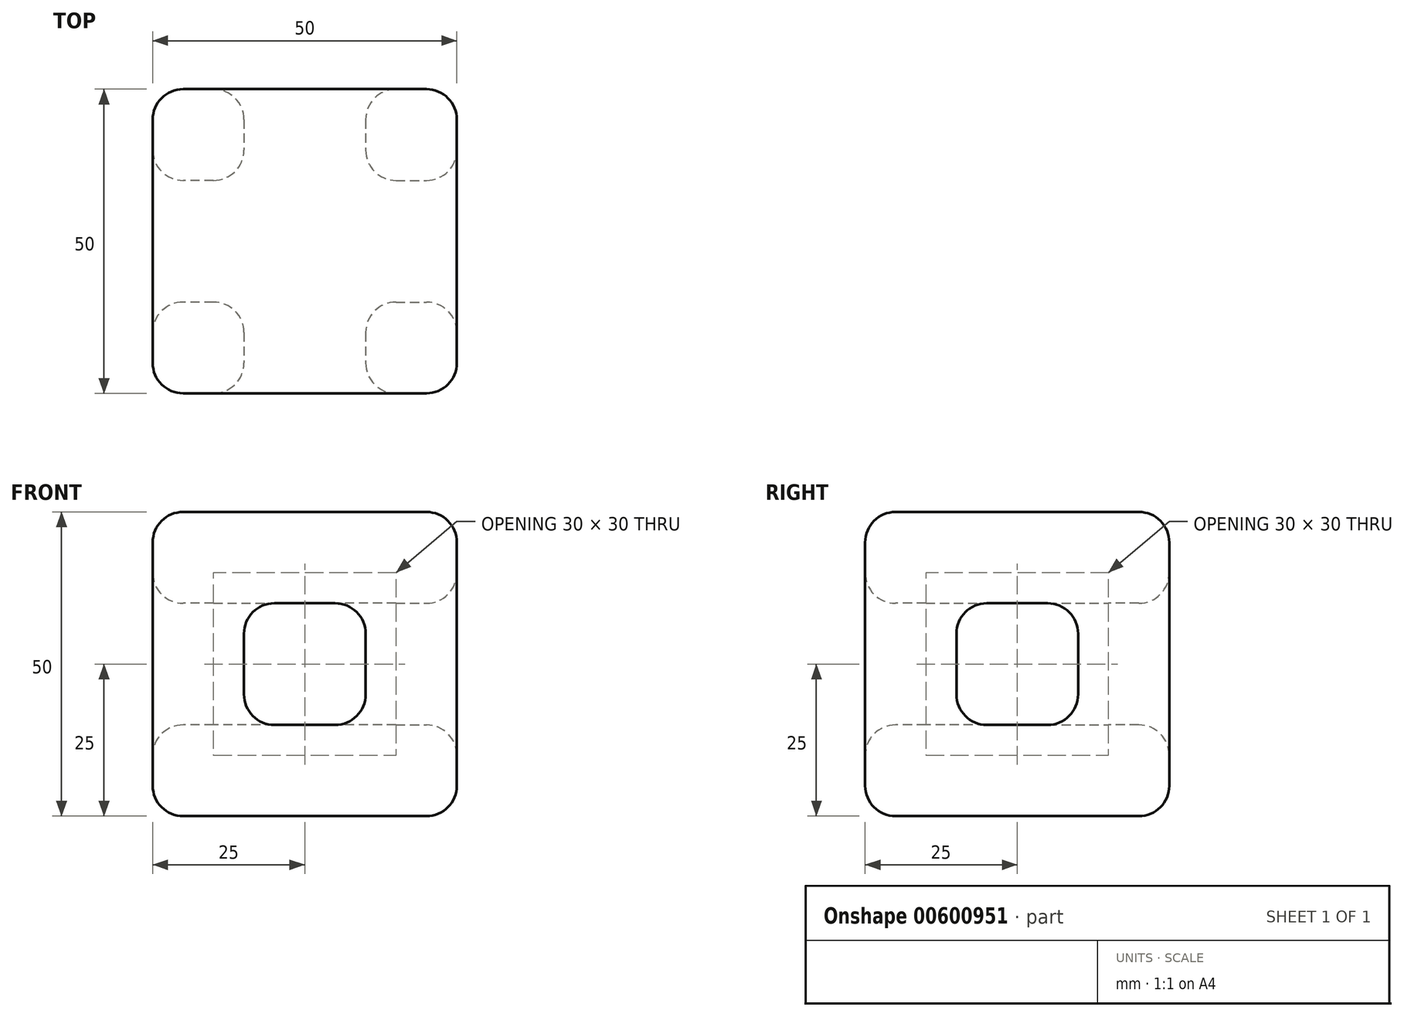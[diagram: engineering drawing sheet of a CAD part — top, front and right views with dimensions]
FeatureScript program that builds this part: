
annotation { "Feature Type Name" : "Feature", "Feature Type Description" : "" }
export const myFeature = defineFeature(function(context is Context, id is Id, definition is map)
    precondition{}
    {
        {
            var Q0;
            Q0=qCreatedBy(makeId("Front.planeOp"),FACE);
            var sketch = newSketch(context, id + "F0", { "sketchPlane" : qUnion([Q0])});
            skLineSegment(sketch, "E0.bottom", {"start": v(25, -25) * mm, "end": v(-25, -25) * mm});
            skLineSegment(sketch, "E0.top", {"start": v(25, 25) * mm, "end": v(-25, 25) * mm});
            skLineSegment(sketch, "E0.left", {"start": v(25, -25) * mm, "end": v(25, 25) * mm});
            skLineSegment(sketch, "E0.right", {"start": v(-25, -25) * mm, "end": v(-25, 25) * mm});
            skPoint(sketch, "E0.middle", {"position": v(0, 0) * mm});
            skSolve(sketch);
        }
        {
            var Q0;
            Q0 = qSketchRegion(id + "F0", true);
            extrude(context, id + "F1", {"entities" : qUnion([Q0]), "endBound" : BoundingType.SYMMETRIC, "depth" : 50 * mm, "offsetDistance" : 25 * mm});
        }
        {
            var Q0;
            Q0=makeQuery(id+"F1.opExtrude","CAP_FACE",FACE,{"disambiguationData":[OSD([sQuery(id+"F0.wireOp",EDGE,"E0.bottom"),sQuery(id+"F0.wireOp",EDGE,"E0.top"),sQuery(id+"F0.wireOp",EDGE,"E0.left"),sQuery(id+"F0.wireOp",EDGE,"E0.right")])],"isStart":false});
            var sketch = newSketch(context, id + "F2", { "sketchPlane" : qUnion([Q0])});
            skLineSegment(sketch, "E1.bottom", {"start": v(-10, 10) * mm, "end": v(10, 10) * mm});
            skLineSegment(sketch, "E1.top", {"start": v(-10, -10) * mm, "end": v(10, -10) * mm});
            skLineSegment(sketch, "E1.left", {"start": v(-10, 10) * mm, "end": v(-10, -10) * mm});
            skLineSegment(sketch, "E1.right", {"start": v(10, 10) * mm, "end": v(10, -10) * mm});
            skPoint(sketch, "E1.middle", {"position": v(0, 0) * mm});
            skSolve(sketch);
        }
        {
            var Q0;
            Q0=makeQuery(id+"F2.imprint","IMPRINT",FACE,{"disambiguationData":[TD([[makeQuery(id+"F2.imprint","IMPRINT",EDGE,{"derivedFrom":sQuery(id+"F2.wireOp",EDGE,"E1.bottom")}),-1.0]])]});
            extrude(context, id + "F3", {"entities" : qUnion([Q0]), "operationType" : NewBodyOperationType.REMOVE, "endBound" : BoundingType.UP_TO_NEXT, "oppositeDirection" : true, "depth" : 25 * mm, "offsetDistance" : 25 * mm});
        }
        {
            var Q0;
            Q0=makeQuery(id+"F1.opExtrude","SWEPT_FACE",FACE,{"disambiguationData":[OSD([sQuery(id+"F0.wireOp",EDGE,"E0.left")])]});
            var sketch = newSketch(context, id + "F4", { "sketchPlane" : qUnion([Q0])});
            skLineSegment(sketch, "E2.bottom", {"start": v(-10, 10) * mm, "end": v(10, 10) * mm});
            skLineSegment(sketch, "E2.top", {"start": v(-10, -10) * mm, "end": v(10, -10) * mm});
            skLineSegment(sketch, "E2.left", {"start": v(-10, 10) * mm, "end": v(-10, -10) * mm});
            skLineSegment(sketch, "E2.right", {"start": v(10, 10) * mm, "end": v(10, -10) * mm});
            skPoint(sketch, "E2.middle", {"position": v(0, 0) * mm});
            skSolve(sketch);
        }
        {
            var Q0;
            Q0=makeQuery(id+"F4.imprint","IMPRINT",FACE,{"disambiguationData":[TD([[makeQuery(id+"F4.imprint","IMPRINT",EDGE,{"derivedFrom":sQuery(id+"F4.wireOp",EDGE,"E2.bottom")}),-1.0]])]});
            extrude(context, id + "F5", {"entities" : qUnion([Q0]), "operationType" : NewBodyOperationType.REMOVE, "endBound" : BoundingType.UP_TO_NEXT, "oppositeDirection" : true, "depth" : 25 * mm, "offsetDistance" : 25 * mm});
        }
        {
            var Q0;
            Q0=makeQuery(id+"F1.opExtrude","SWEPT_FACE",FACE,{"disambiguationData":[OSD([sQuery(id+"F0.wireOp",EDGE,"E0.right")])]});
            var sketch = newSketch(context, id + "F6", { "sketchPlane" : qUnion([Q0])});
            skLineSegment(sketch, "E3.bottom", {"start": v(-10, 10) * mm, "end": v(10, 10) * mm});
            skLineSegment(sketch, "E3.top", {"start": v(-10, -10) * mm, "end": v(10, -10) * mm});
            skLineSegment(sketch, "E3.left", {"start": v(-10, 10) * mm, "end": v(-10, -10) * mm});
            skLineSegment(sketch, "E3.right", {"start": v(10, 10) * mm, "end": v(10, -10) * mm});
            skPoint(sketch, "E3.middle", {"position": v(0, 0) * mm});
            skSolve(sketch);
        }
        {
            var Q0;
            Q0=makeQuery(id+"F6.imprint","IMPRINT",FACE,{"disambiguationData":[TD([[makeQuery(id+"F6.imprint","IMPRINT",EDGE,{"derivedFrom":sQuery(id+"F6.wireOp",EDGE,"E3.bottom")}),-1.0]])]});
            extrude(context, id + "F7", {"entities" : qUnion([Q0]), "operationType" : NewBodyOperationType.REMOVE, "endBound" : BoundingType.UP_TO_NEXT, "oppositeDirection" : true, "depth" : 25 * mm, "offsetDistance" : 25 * mm});
        }
        {
            var Q0;
            Q0=makeQuery(id+"F7.boolean.opBoolean","COPY",EDGE,{"derivedFrom":makeQuery(id+"F7.opExtrude","SWEPT_EDGE",EDGE,{"disambiguationData":[OSD([sQuery(id+"F6.wireOp",EDGE,"E3.bottom"),sQuery(id+"F6.wireOp",EDGE,"E3.right")])]})});
            var Q1;
            Q1=makeQuery(id+"F5.boolean.opBoolean","COPY",EDGE,{"derivedFrom":makeQuery(id+"F5.opExtrude","SWEPT_EDGE",EDGE,{"disambiguationData":[OSD([sQuery(id+"F4.wireOp",EDGE,"E2.bottom"),sQuery(id+"F4.wireOp",EDGE,"E2.left")])]})});
            var Q2;
            Q2=makeQuery(id+"F3.boolean.opBoolean","COPY",EDGE,{"derivedFrom":makeQuery(id+"F3.opExtrude","CAP_EDGE",EDGE,{"disambiguationData":[OSD([sQuery(id+"F2.wireOp",EDGE,"E1.right")])],"isStart":true})});
            var Q3;
            Q3=makeQuery(id+"F1.opExtrude","CAP_EDGE",EDGE,{"disambiguationData":[OSD([sQuery(id+"F0.wireOp",EDGE,"E0.bottom")])],"isStart":false});
            var Q4;
            Q4=makeQuery(id+"F1.opExtrude","CAP_FACE",FACE,{"disambiguationData":[OSD([sQuery(id+"F0.wireOp",EDGE,"E0.bottom"),sQuery(id+"F0.wireOp",EDGE,"E0.top"),sQuery(id+"F0.wireOp",EDGE,"E0.left"),sQuery(id+"F0.wireOp",EDGE,"E0.right")])],"isStart":false});
            var Q5;
            Q5=makeQuery(id+"F7.boolean.opBoolean","COPY",EDGE,{"derivedFrom":makeQuery(id+"F7.opExtrude","SWEPT_EDGE",EDGE,{"disambiguationData":[OSD([sQuery(id+"F6.wireOp",EDGE,"E3.top"),sQuery(id+"F6.wireOp",EDGE,"E3.right")])]})});
            var Q6;
            Q6=makeQuery(id+"F3.boolean.opBoolean","COPY",EDGE,{"derivedFrom":makeQuery(id+"F3.opExtrude","CAP_EDGE",EDGE,{"disambiguationData":[OSD([sQuery(id+"F2.wireOp",EDGE,"E1.bottom")])],"isStart":true})});
            var Q7;
            Q7=makeQuery(id+"F1.opExtrude","SWEPT_EDGE",EDGE,{"disambiguationData":[OSD([sQuery(id+"F0.wireOp",EDGE,"E0.top"),sQuery(id+"F0.wireOp",EDGE,"E0.right")])]});
            var Q8;
            Q8=makeQuery(id+"F1.opExtrude","CAP_EDGE",EDGE,{"disambiguationData":[OSD([sQuery(id+"F0.wireOp",EDGE,"E0.right")])],"isStart":false});
            var Q9;
            Q9=makeQuery(id+"F3.boolean.opBoolean","COPY",EDGE,{"derivedFrom":makeQuery(id+"F3.opExtrude","CAP_EDGE",EDGE,{"disambiguationData":[OSD([sQuery(id+"F2.wireOp",EDGE,"E1.top")])],"isStart":true})});
            var Q10;
            Q10=makeQuery(id+"F1.opExtrude","CAP_EDGE",EDGE,{"disambiguationData":[OSD([sQuery(id+"F0.wireOp",EDGE,"E0.top")])],"isStart":false});
            var Q11;
            Q11=makeQuery(id+"F5.boolean.opBoolean","COPY",EDGE,{"derivedFrom":makeQuery(id+"F5.opExtrude","SWEPT_EDGE",EDGE,{"disambiguationData":[OSD([sQuery(id+"F4.wireOp",EDGE,"E2.top"),sQuery(id+"F4.wireOp",EDGE,"E2.left")])]})});
            var Q12;
            Q12=makeQuery(id+"F3.boolean.opBoolean","COPY",EDGE,{"derivedFrom":makeQuery(id+"F3.opExtrude","CAP_EDGE",EDGE,{"disambiguationData":[OSD([sQuery(id+"F2.wireOp",EDGE,"E1.left")])],"isStart":true})});
            var Q13;
            Q13=makeQuery(id+"F1.opExtrude","CAP_EDGE",EDGE,{"disambiguationData":[OSD([sQuery(id+"F0.wireOp",EDGE,"E0.left")])],"isStart":false});
            var Q14;
            Q14=makeQuery(id+"F1.opExtrude","CAP_EDGE",EDGE,{"disambiguationData":[OSD([sQuery(id+"F0.wireOp",EDGE,"E0.top")])],"isStart":true});
            var Q15;
            Q15=makeQuery(id+"F5.boolean.opBoolean","COPY",FACE,{"derivedFrom":makeQuery(id+"F5.opExtrude","SWEPT_FACE",FACE,{"disambiguationData":[OSD([sQuery(id+"F4.wireOp",EDGE,"E2.left")])]})});
            var Q16;
            {var subQ0=sQuery(id+"F2.wireOp",EDGE,"E1.top");var subQ1=sQuery(id+"F2.wireOp",EDGE,"E1.right");Q16=makeQuery(id+"F5.boolean.opBoolean","SPLIT",EDGE,{"disambiguationData":[TD([makeQuery(id+"F5.opExtrude","SWEPT_FACE",FACE,{"disambiguationData":[OSD([sQuery(id+"F4.wireOp",EDGE,"E2.left")])]})])],"derivedFrom":makeQuery(id+"F3.boolean.opBoolean","COPY",EDGE,{"derivedFrom":makeQuery(id+"F3.opExtrude","SWEPT_EDGE",EDGE,{"disambiguationData":[OSD([subQ0,subQ1])]})})});}
            var Q17;
            Q17=makeQuery(id+"F7.boolean.opBoolean","COPY",EDGE,{"derivedFrom":makeQuery(id+"F7.opExtrude","SWEPT_EDGE",EDGE,{"disambiguationData":[OSD([sQuery(id+"F6.wireOp",EDGE,"E3.top"),sQuery(id+"F6.wireOp",EDGE,"E3.left")])]})});
            var Q18;
            Q18=makeQuery(id+"F7.boolean.opBoolean","COPY",EDGE,{"derivedFrom":makeQuery(id+"F7.opExtrude","CAP_EDGE",EDGE,{"disambiguationData":[OSD([sQuery(id+"F6.wireOp",EDGE,"E3.right")])],"isStart":true})});
            var Q19;
            Q19=makeQuery(id+"F5.boolean.opBoolean","COPY",EDGE,{"derivedFrom":makeQuery(id+"F5.opExtrude","SWEPT_EDGE",EDGE,{"disambiguationData":[OSD([sQuery(id+"F4.wireOp",EDGE,"E2.bottom"),sQuery(id+"F4.wireOp",EDGE,"E2.right")])]})});
            var Q20;
            Q20=makeQuery(id+"F1.opExtrude","SWEPT_EDGE",EDGE,{"disambiguationData":[OSD([sQuery(id+"F0.wireOp",EDGE,"E0.bottom"),sQuery(id+"F0.wireOp",EDGE,"E0.left")])]});
            var Q21;
            {var subQ0=sQuery(id+"F2.wireOp",EDGE,"E1.left");var subQ1=sQuery(id+"F2.wireOp",EDGE,"E1.bottom");Q21=makeQuery(id+"F7.boolean.opBoolean","SPLIT",EDGE,{"disambiguationData":[TD([makeQuery(id+"F7.opExtrude","SWEPT_FACE",FACE,{"disambiguationData":[OSD([sQuery(id+"F6.wireOp",EDGE,"E3.right")])]})])],"derivedFrom":makeQuery(id+"F3.boolean.opBoolean","COPY",EDGE,{"derivedFrom":makeQuery(id+"F3.opExtrude","SWEPT_EDGE",EDGE,{"disambiguationData":[OSD([subQ1,subQ0])]})})});}
            var Q22;
            Q22=makeQuery(id+"F7.boolean.opBoolean","COPY",EDGE,{"derivedFrom":makeQuery(id+"F7.opExtrude","SWEPT_EDGE",EDGE,{"disambiguationData":[OSD([sQuery(id+"F6.wireOp",EDGE,"E3.bottom"),sQuery(id+"F6.wireOp",EDGE,"E3.left")])]})});
            var Q23;
            Q23=makeQuery(id+"F3.boolean.opBoolean","COPY",EDGE,{"derivedFrom":makeQuery(id+"F3.opExtrude","TWEAK_EDGE",EDGE,{"derivedFrom":[makeQuery(id+"F1.opExtrude","CAP_FACE",FACE,{"disambiguationData":[OSD([sQuery(id+"F0.wireOp",EDGE,"E0.bottom"),sQuery(id+"F0.wireOp",EDGE,"E0.top"),sQuery(id+"F0.wireOp",EDGE,"E0.left"),sQuery(id+"F0.wireOp",EDGE,"E0.right")])],"isStart":true}),makeQuery(id+"F2.imprint","IMPRINT",EDGE,{"derivedFrom":sQuery(id+"F2.wireOp",EDGE,"E1.top")})]})});
            var Q24;
            Q24=makeQuery(id+"F5.boolean.opBoolean","COPY",EDGE,{"derivedFrom":makeQuery(id+"F5.opExtrude","CAP_EDGE",EDGE,{"disambiguationData":[OSD([sQuery(id+"F4.wireOp",EDGE,"E2.left")])],"isStart":true})});
            var Q25;
            Q25=makeQuery(id+"F7.boolean.opBoolean","COPY",FACE,{"derivedFrom":makeQuery(id+"F7.opExtrude","SWEPT_FACE",FACE,{"disambiguationData":[OSD([sQuery(id+"F6.wireOp",EDGE,"E3.right")])]})});
            var Q26;
            Q26=makeQuery(id+"F3.boolean.opBoolean","COPY",EDGE,{"derivedFrom":makeQuery(id+"F3.opExtrude","TWEAK_EDGE",EDGE,{"derivedFrom":[makeQuery(id+"F1.opExtrude","CAP_FACE",FACE,{"disambiguationData":[OSD([sQuery(id+"F0.wireOp",EDGE,"E0.bottom"),sQuery(id+"F0.wireOp",EDGE,"E0.top"),sQuery(id+"F0.wireOp",EDGE,"E0.left"),sQuery(id+"F0.wireOp",EDGE,"E0.right")])],"isStart":true}),makeQuery(id+"F2.imprint","IMPRINT",EDGE,{"derivedFrom":sQuery(id+"F2.wireOp",EDGE,"E1.bottom")})]})});
            var Q27;
            Q27=makeQuery(id+"F1.opExtrude","CAP_EDGE",EDGE,{"disambiguationData":[OSD([sQuery(id+"F0.wireOp",EDGE,"E0.bottom")])],"isStart":true});
            var Q28;
            Q28=makeQuery(id+"F5.boolean.opBoolean","COPY",EDGE,{"derivedFrom":makeQuery(id+"F5.opExtrude","TWEAK_EDGE",EDGE,{"derivedFrom":[makeQuery(id+"F3.boolean.opBoolean","COPY",FACE,{"derivedFrom":makeQuery(id+"F3.opExtrude","SWEPT_FACE",FACE,{"disambiguationData":[OSD([sQuery(id+"F2.wireOp",EDGE,"E1.right")])]})}),makeQuery(id+"F4.imprint","IMPRINT",EDGE,{"derivedFrom":sQuery(id+"F4.wireOp",EDGE,"E2.left")})]})});
            var Q29;
            Q29=makeQuery(id+"F5.boolean.opBoolean","COPY",EDGE,{"derivedFrom":makeQuery(id+"F5.opExtrude","SWEPT_EDGE",EDGE,{"disambiguationData":[OSD([sQuery(id+"F4.wireOp",EDGE,"E2.top"),sQuery(id+"F4.wireOp",EDGE,"E2.right")])]})});
            var Q30;
            {var subQ0=sQuery(id+"F2.wireOp",EDGE,"E1.bottom");var subQ1=sQuery(id+"F2.wireOp",EDGE,"E1.right");Q30=makeQuery(id+"F5.boolean.opBoolean","SPLIT",EDGE,{"disambiguationData":[TD([makeQuery(id+"F5.opExtrude","SWEPT_FACE",FACE,{"disambiguationData":[OSD([sQuery(id+"F4.wireOp",EDGE,"E2.left")])]})])],"derivedFrom":makeQuery(id+"F3.boolean.opBoolean","COPY",EDGE,{"derivedFrom":makeQuery(id+"F3.opExtrude","SWEPT_EDGE",EDGE,{"disambiguationData":[OSD([subQ0,subQ1])]})})});}
            var Q31;
            Q31=makeQuery(id+"F1.opExtrude","SWEPT_EDGE",EDGE,{"disambiguationData":[OSD([sQuery(id+"F0.wireOp",EDGE,"E0.bottom"),sQuery(id+"F0.wireOp",EDGE,"E0.right")])]});
            var Q32;
            Q32=makeQuery(id+"F1.opExtrude","CAP_FACE",FACE,{"disambiguationData":[OSD([sQuery(id+"F0.wireOp",EDGE,"E0.bottom"),sQuery(id+"F0.wireOp",EDGE,"E0.top"),sQuery(id+"F0.wireOp",EDGE,"E0.left"),sQuery(id+"F0.wireOp",EDGE,"E0.right")])],"isStart":true});
            var Q33;
            Q33=makeQuery(id+"F7.boolean.opBoolean","COPY",EDGE,{"derivedFrom":makeQuery(id+"F7.opExtrude","TWEAK_EDGE",EDGE,{"derivedFrom":[makeQuery(id+"F3.boolean.opBoolean","COPY",FACE,{"derivedFrom":makeQuery(id+"F3.opExtrude","SWEPT_FACE",FACE,{"disambiguationData":[OSD([sQuery(id+"F2.wireOp",EDGE,"E1.left")])]})}),makeQuery(id+"F6.imprint","IMPRINT",EDGE,{"derivedFrom":sQuery(id+"F6.wireOp",EDGE,"E3.right")})]})});
            var Q34;
            {var subQ0=sQuery(id+"F2.wireOp",EDGE,"E1.left");var subQ1=sQuery(id+"F2.wireOp",EDGE,"E1.top");Q34=makeQuery(id+"F7.boolean.opBoolean","SPLIT",EDGE,{"disambiguationData":[TD([makeQuery(id+"F7.opExtrude","SWEPT_FACE",FACE,{"disambiguationData":[OSD([sQuery(id+"F6.wireOp",EDGE,"E3.right")])]})])],"derivedFrom":makeQuery(id+"F3.boolean.opBoolean","COPY",EDGE,{"derivedFrom":makeQuery(id+"F3.opExtrude","SWEPT_EDGE",EDGE,{"disambiguationData":[OSD([subQ1,subQ0])]})})});}
            var Q35;
            Q35=makeQuery(id+"F1.opExtrude","CAP_EDGE",EDGE,{"disambiguationData":[OSD([sQuery(id+"F0.wireOp",EDGE,"E0.left")])],"isStart":true});
            var Q36;
            Q36=makeQuery(id+"F1.opExtrude","CAP_EDGE",EDGE,{"disambiguationData":[OSD([sQuery(id+"F0.wireOp",EDGE,"E0.right")])],"isStart":true});
            var Q37;
            Q37=makeQuery(id+"F1.opExtrude","SWEPT_EDGE",EDGE,{"disambiguationData":[OSD([sQuery(id+"F0.wireOp",EDGE,"E0.top"),sQuery(id+"F0.wireOp",EDGE,"E0.left")])]});
            var Q38;
            Q38=makeQuery(id+"F7.boolean.opBoolean","COPY",EDGE,{"derivedFrom":makeQuery(id+"F7.opExtrude","CAP_EDGE",EDGE,{"disambiguationData":[OSD([sQuery(id+"F6.wireOp",EDGE,"E3.bottom")])],"isStart":true})});
            var Q39;
            Q39=makeQuery(id+"F7.boolean.opBoolean","COPY",EDGE,{"derivedFrom":makeQuery(id+"F7.opExtrude","CAP_EDGE",EDGE,{"disambiguationData":[OSD([sQuery(id+"F6.wireOp",EDGE,"E3.left")])],"isStart":true})});
            var Q40;
            Q40=makeQuery(id+"F5.boolean.opBoolean","COPY",EDGE,{"derivedFrom":makeQuery(id+"F5.opExtrude","TWEAK_EDGE",EDGE,{"derivedFrom":[makeQuery(id+"F3.boolean.opBoolean","COPY",FACE,{"derivedFrom":makeQuery(id+"F3.opExtrude","SWEPT_FACE",FACE,{"disambiguationData":[OSD([sQuery(id+"F2.wireOp",EDGE,"E1.right")])]})}),makeQuery(id+"F4.imprint","IMPRINT",EDGE,{"derivedFrom":sQuery(id+"F4.wireOp",EDGE,"E2.right")})]})});
            var Q41;
            Q41=makeQuery(id+"F7.boolean.opBoolean","COPY",EDGE,{"derivedFrom":makeQuery(id+"F7.opExtrude","TWEAK_EDGE",EDGE,{"derivedFrom":[makeQuery(id+"F3.boolean.opBoolean","COPY",FACE,{"derivedFrom":makeQuery(id+"F3.opExtrude","SWEPT_FACE",FACE,{"disambiguationData":[OSD([sQuery(id+"F2.wireOp",EDGE,"E1.left")])]})}),makeQuery(id+"F6.imprint","IMPRINT",EDGE,{"derivedFrom":sQuery(id+"F6.wireOp",EDGE,"E3.left")})]})});
            var Q42;
            {var subQ0=sQuery(id+"F2.wireOp",EDGE,"E1.left");var subQ1=sQuery(id+"F2.wireOp",EDGE,"E1.bottom");Q42=makeQuery(id+"F7.boolean.opBoolean","SPLIT",EDGE,{"disambiguationData":[TD([makeQuery(id+"F7.opExtrude","SWEPT_FACE",FACE,{"disambiguationData":[OSD([sQuery(id+"F6.wireOp",EDGE,"E3.left")])]})])],"derivedFrom":makeQuery(id+"F3.boolean.opBoolean","COPY",EDGE,{"derivedFrom":makeQuery(id+"F3.opExtrude","SWEPT_EDGE",EDGE,{"disambiguationData":[OSD([subQ1,subQ0])]})})});}
            var Q43;
            {var subQ0=sQuery(id+"F2.wireOp",EDGE,"E1.right");var subQ1=sQuery(id+"F2.wireOp",EDGE,"E1.bottom");Q43=makeQuery(id+"F5.boolean.opBoolean","SPLIT",EDGE,{"disambiguationData":[TD([makeQuery(id+"F5.opExtrude","SWEPT_FACE",FACE,{"disambiguationData":[OSD([sQuery(id+"F4.wireOp",EDGE,"E2.right")])]})])],"derivedFrom":makeQuery(id+"F3.boolean.opBoolean","COPY",EDGE,{"derivedFrom":makeQuery(id+"F3.opExtrude","SWEPT_EDGE",EDGE,{"disambiguationData":[OSD([subQ1,subQ0])]})})});}
            var Q44;
            Q44=makeQuery(id+"F7.boolean.opBoolean","COPY",EDGE,{"derivedFrom":makeQuery(id+"F7.opExtrude","CAP_EDGE",EDGE,{"disambiguationData":[OSD([sQuery(id+"F6.wireOp",EDGE,"E3.top")])],"isStart":true})});
            var Q45;
            Q45=makeQuery(id+"F7.boolean.opBoolean","COPY",FACE,{"derivedFrom":makeQuery(id+"F7.opExtrude","SWEPT_FACE",FACE,{"disambiguationData":[OSD([sQuery(id+"F6.wireOp",EDGE,"E3.left")])]})});
            var Q46;
            Q46=makeQuery(id+"F5.boolean.opBoolean","COPY",FACE,{"derivedFrom":makeQuery(id+"F5.opExtrude","SWEPT_FACE",FACE,{"disambiguationData":[OSD([sQuery(id+"F4.wireOp",EDGE,"E2.right")])]})});
            var Q47;
            Q47=makeQuery(id+"F5.boolean.opBoolean","COPY",EDGE,{"derivedFrom":makeQuery(id+"F5.opExtrude","CAP_EDGE",EDGE,{"disambiguationData":[OSD([sQuery(id+"F4.wireOp",EDGE,"E2.top")])],"isStart":true})});
            var Q48;
            Q48=makeQuery(id+"F1.opExtrude","SWEPT_FACE",FACE,{"disambiguationData":[OSD([sQuery(id+"F0.wireOp",EDGE,"E0.right")])]});
            var Q49;
            Q49=makeQuery(id+"F7.boolean.opBoolean","MERGE",FACE,{"derivedFrom":[makeQuery(id+"F5.boolean.opBoolean","MERGE",FACE,{"derivedFrom":[makeQuery(id+"F3.boolean.opBoolean","COPY",FACE,{"derivedFrom":makeQuery(id+"F3.opExtrude","SWEPT_FACE",FACE,{"disambiguationData":[OSD([sQuery(id+"F2.wireOp",EDGE,"E1.top")])]})}),makeQuery(id+"F5.opExtrude","SWEPT_FACE",FACE,{"disambiguationData":[OSD([sQuery(id+"F4.wireOp",EDGE,"E2.top")])]})]}),makeQuery(id+"F7.opExtrude","SWEPT_FACE",FACE,{"disambiguationData":[OSD([sQuery(id+"F6.wireOp",EDGE,"E3.top")])]})]});
            var Q50;
            Q50=makeQuery(id+"F5.boolean.opBoolean","COPY",EDGE,{"derivedFrom":makeQuery(id+"F5.opExtrude","CAP_EDGE",EDGE,{"disambiguationData":[OSD([sQuery(id+"F4.wireOp",EDGE,"E2.bottom")])],"isStart":true})});
            var Q51;
            Q51=makeQuery(id+"F1.opExtrude","SWEPT_FACE",FACE,{"disambiguationData":[OSD([sQuery(id+"F0.wireOp",EDGE,"E0.top")])]});
            var Q52;
            Q52=makeQuery(id+"F1.opExtrude","SWEPT_FACE",FACE,{"disambiguationData":[OSD([sQuery(id+"F0.wireOp",EDGE,"E0.bottom")])]});
            var Q53;
            Q53=makeQuery(id+"F1.opExtrude","SWEPT_FACE",FACE,{"disambiguationData":[OSD([sQuery(id+"F0.wireOp",EDGE,"E0.left")])]});
            var Q54;
            Q54=makeQuery(id+"F7.boolean.opBoolean","MERGE",FACE,{"derivedFrom":[makeQuery(id+"F5.boolean.opBoolean","MERGE",FACE,{"derivedFrom":[makeQuery(id+"F3.boolean.opBoolean","COPY",FACE,{"derivedFrom":makeQuery(id+"F3.opExtrude","SWEPT_FACE",FACE,{"disambiguationData":[OSD([sQuery(id+"F2.wireOp",EDGE,"E1.bottom")])]})}),makeQuery(id+"F5.opExtrude","SWEPT_FACE",FACE,{"disambiguationData":[OSD([sQuery(id+"F4.wireOp",EDGE,"E2.bottom")])]})]}),makeQuery(id+"F7.opExtrude","SWEPT_FACE",FACE,{"disambiguationData":[OSD([sQuery(id+"F6.wireOp",EDGE,"E3.bottom")])]})]});
            var Q55;
            Q55=makeQuery(id+"F5.boolean.opBoolean","COPY",EDGE,{"derivedFrom":makeQuery(id+"F5.opExtrude","CAP_EDGE",EDGE,{"disambiguationData":[OSD([sQuery(id+"F4.wireOp",EDGE,"E2.right")])],"isStart":true})});
            var Q56;
            {var subQ0=sQuery(id+"F2.wireOp",EDGE,"E1.right");var subQ1=sQuery(id+"F2.wireOp",EDGE,"E1.top");Q56=makeQuery(id+"F5.boolean.opBoolean","SPLIT",EDGE,{"disambiguationData":[TD([makeQuery(id+"F5.opExtrude","SWEPT_FACE",FACE,{"disambiguationData":[OSD([sQuery(id+"F4.wireOp",EDGE,"E2.right")])]})])],"derivedFrom":makeQuery(id+"F3.boolean.opBoolean","COPY",EDGE,{"derivedFrom":makeQuery(id+"F3.opExtrude","SWEPT_EDGE",EDGE,{"disambiguationData":[OSD([subQ1,subQ0])]})})});}
            var Q57;
            Q57=makeQuery(id+"F3.boolean.opBoolean","COPY",EDGE,{"derivedFrom":makeQuery(id+"F3.opExtrude","TWEAK_EDGE",EDGE,{"derivedFrom":[makeQuery(id+"F1.opExtrude","CAP_FACE",FACE,{"disambiguationData":[OSD([sQuery(id+"F0.wireOp",EDGE,"E0.bottom"),sQuery(id+"F0.wireOp",EDGE,"E0.top"),sQuery(id+"F0.wireOp",EDGE,"E0.left"),sQuery(id+"F0.wireOp",EDGE,"E0.right")])],"isStart":true}),makeQuery(id+"F2.imprint","IMPRINT",EDGE,{"derivedFrom":sQuery(id+"F2.wireOp",EDGE,"E1.right")})]})});
            var Q58;
            {var subQ0=sQuery(id+"F2.wireOp",EDGE,"E1.top");var subQ1=sQuery(id+"F2.wireOp",EDGE,"E1.left");Q58=makeQuery(id+"F7.boolean.opBoolean","SPLIT",EDGE,{"disambiguationData":[TD([makeQuery(id+"F7.opExtrude","SWEPT_FACE",FACE,{"disambiguationData":[OSD([sQuery(id+"F6.wireOp",EDGE,"E3.left")])]})])],"derivedFrom":makeQuery(id+"F3.boolean.opBoolean","COPY",EDGE,{"derivedFrom":makeQuery(id+"F3.opExtrude","SWEPT_EDGE",EDGE,{"disambiguationData":[OSD([subQ0,subQ1])]})})});}
            var Q59;
            Q59=makeQuery(id+"F3.boolean.opBoolean","COPY",EDGE,{"derivedFrom":makeQuery(id+"F3.opExtrude","TWEAK_EDGE",EDGE,{"derivedFrom":[makeQuery(id+"F1.opExtrude","CAP_FACE",FACE,{"disambiguationData":[OSD([sQuery(id+"F0.wireOp",EDGE,"E0.bottom"),sQuery(id+"F0.wireOp",EDGE,"E0.top"),sQuery(id+"F0.wireOp",EDGE,"E0.left"),sQuery(id+"F0.wireOp",EDGE,"E0.right")])],"isStart":true}),makeQuery(id+"F2.imprint","IMPRINT",EDGE,{"derivedFrom":sQuery(id+"F2.wireOp",EDGE,"E1.left")})]})});
            var Q60;
            Q60=makeQuery(id+"F7.boolean.opBoolean","SPLIT",FACE,{"disambiguationData":[TD([makeQuery(id+"F7.opExtrude","SWEPT_FACE",FACE,{"disambiguationData":[OSD([sQuery(id+"F6.wireOp",EDGE,"E3.right")])]})])],"derivedFrom":makeQuery(id+"F3.boolean.opBoolean","COPY",FACE,{"derivedFrom":makeQuery(id+"F3.opExtrude","SWEPT_FACE",FACE,{"disambiguationData":[OSD([sQuery(id+"F2.wireOp",EDGE,"E1.left")])]})})});
            var Q61;
            Q61=makeQuery(id+"F5.boolean.opBoolean","SPLIT",FACE,{"disambiguationData":[TD([makeQuery(id+"F5.opExtrude","SWEPT_FACE",FACE,{"disambiguationData":[OSD([sQuery(id+"F4.wireOp",EDGE,"E2.left")])]})])],"derivedFrom":makeQuery(id+"F3.boolean.opBoolean","COPY",FACE,{"derivedFrom":makeQuery(id+"F3.opExtrude","SWEPT_FACE",FACE,{"disambiguationData":[OSD([sQuery(id+"F2.wireOp",EDGE,"E1.right")])]})})});
            var Q62;
            Q62=makeQuery(id+"F7.boolean.opBoolean","SPLIT",FACE,{"disambiguationData":[TD([makeQuery(id+"F7.opExtrude","SWEPT_FACE",FACE,{"disambiguationData":[OSD([sQuery(id+"F6.wireOp",EDGE,"E3.left")])]})])],"derivedFrom":makeQuery(id+"F3.boolean.opBoolean","COPY",FACE,{"derivedFrom":makeQuery(id+"F3.opExtrude","SWEPT_FACE",FACE,{"disambiguationData":[OSD([sQuery(id+"F2.wireOp",EDGE,"E1.left")])]})})});
            var Q63;
            Q63=makeQuery(id+"F5.boolean.opBoolean","SPLIT",FACE,{"disambiguationData":[TD([makeQuery(id+"F5.opExtrude","SWEPT_FACE",FACE,{"disambiguationData":[OSD([sQuery(id+"F4.wireOp",EDGE,"E2.right")])]})])],"derivedFrom":makeQuery(id+"F3.boolean.opBoolean","COPY",FACE,{"derivedFrom":makeQuery(id+"F3.opExtrude","SWEPT_FACE",FACE,{"disambiguationData":[OSD([sQuery(id+"F2.wireOp",EDGE,"E1.right")])]})})});
            fillet(context, id + "F8", {"entities" : qUnion([Q0, Q1, Q2, Q3, Q4, Q5, Q6, Q7, Q8, Q9, Q10, Q11, Q12, Q13, Q14, Q15, Q16, Q17, Q18, Q19, Q20, Q21, Q22, Q23, Q24, Q25, Q26, Q27, Q28, Q29, Q30, Q31, Q32, Q33, Q34, Q35, Q36, Q37, Q38, Q39, Q40, Q41, Q42, Q43, Q44, Q45, Q46, Q47, Q48, Q49, Q50, Q51, Q52, Q53, Q54, Q55, Q56, Q57, Q58, Q59, Q60, Q61, Q62, Q63]), "radius" : 5 * mm, "tangentPropagation" : true, "allowEdgeOverflow" : false});
        }
    });
